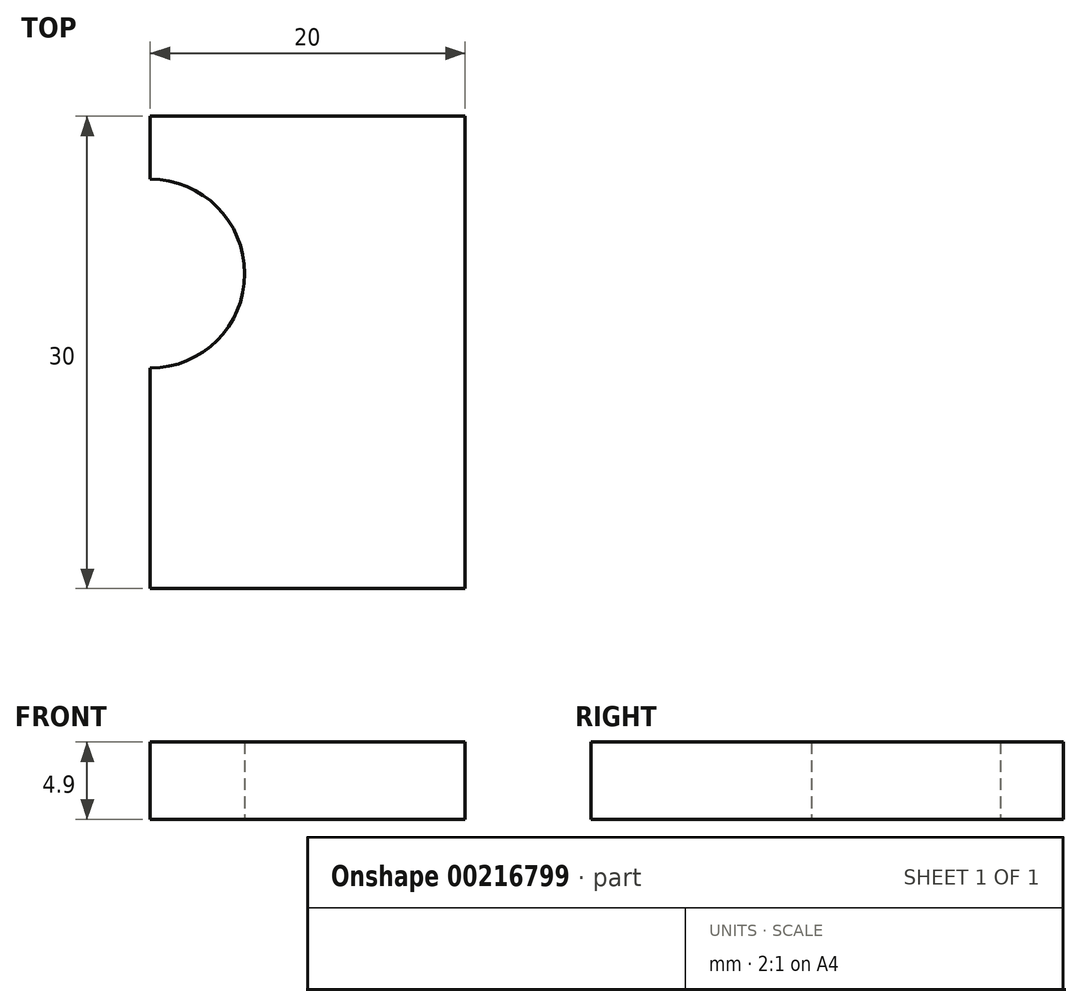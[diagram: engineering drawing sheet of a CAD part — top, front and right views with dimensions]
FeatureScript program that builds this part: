
annotation { "Feature Type Name" : "Feature", "Feature Type Description" : "" }
export const myFeature = defineFeature(function(context is Context, id is Id, definition is map)
    precondition{}
    {
        {
            var Q0;
            Q0=qCreatedBy(makeId("Top.planeOp"),FACE);
            var sketch = newSketch(context, id + "F0", { "sketchPlane" : qUnion([Q0])});
            skLineSegment(sketch, "E0.bottom", {"start": v(10, 15) * mm, "end": v(-10, 15) * mm});
            skLineSegment(sketch, "E0.top", {"start": v(10, -15) * mm, "end": v(-10, -15) * mm});
            skLineSegment(sketch, "E0.left", {"start": v(10, 15) * mm, "end": v(10, -15) * mm});
            skLineSegment(sketch, "E0.right", {"start": v(-10, 15) * mm, "end": v(-10, -15) * mm});
            skPoint(sketch, "E0.middle", {"position": v(0, 0) * mm});
            skCircle(sketch, "E1", {"center": v(-10, 5) * mm, "radius": 6 * mm});
            skSolve(sketch);
        }
        {
            var Q0;
            {var subQ1=sQuery(id+"F0.wireOp",EDGE,"E0.bottom");Q0=makeQuery(id+"F0.imprint","IMPRINT",FACE,{"disambiguationData":[TD([[makeQuery(id+"F0.imprint","IMPRINT",EDGE,{"derivedFrom":subQ1}),1.0]])]});}
            extrude(context, id + "F1", {"entities" : qUnion([Q0]), "depth" : 4.9 * mm});
        }
    });
